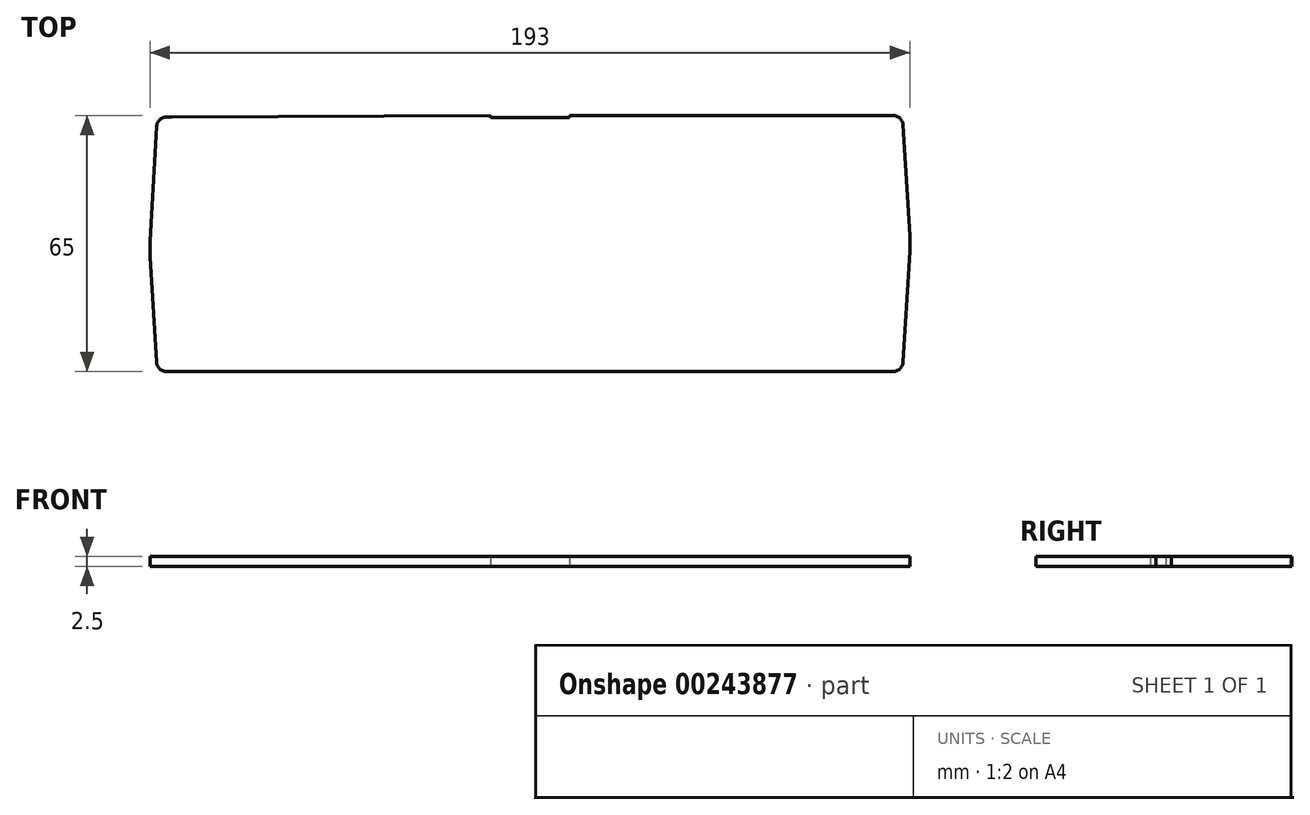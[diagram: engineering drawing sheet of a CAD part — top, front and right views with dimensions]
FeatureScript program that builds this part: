
annotation { "Feature Type Name" : "Feature", "Feature Type Description" : "" }
export const myFeature = defineFeature(function(context is Context, id is Id, definition is map)
    precondition{}
    {
        {
            var Q0;
            Q0=qCreatedBy(makeId("Top.planeOp"),FACE);
            var sketch = newSketch(context, id + "F0", { "sketchPlane" : qUnion([Q0])});
            skLineSegment(sketch, "E0", {"start": v(0, 0) * mm, "end": v(96.5, 0) * mm, "construction": true});
            skLineSegment(sketch, "E1", {"start": v(0, 0) * mm, "end": v(0, 32) * mm, "construction": true});
            skLineSegment(sketch, "E2", {"start": v(0, 0) * mm, "end": v(0, -32.5) * mm, "construction": true});
            skLineSegment(sketch, "E3", {"start": v(0, 32) * mm, "end": v(10, 32) * mm});
            skLineSegment(sketch, "E4", {"start": v(0, 32) * mm, "end": v(-10, 32) * mm});
            skLineSegment(sketch, "E5", {"start": v(-10, 32) * mm, "end": v(-10, 32.5) * mm});
            skLineSegment(sketch, "E6", {"start": v(10, 32) * mm, "end": v(10, 32.5) * mm});
            skLineSegment(sketch, "E7", {"start": v(0, -32.5) * mm, "end": v(92.28, -32.5) * mm});
            skLineSegment(sketch, "E8", {"start": v(0, -32.5) * mm, "end": v(-92.37, -32.5) * mm});
            skLineSegment(sketch, "E9", {"start": v(-96.5, -1.4) * mm, "end": v(-96.5, -3.4) * mm});
            skLineSegment(sketch, "E10", {"start": v(96.5, 0) * mm, "end": v(96.5, -2) * mm});
            skLineSegment(sketch, "E11", {"start": v(96.5, 0) * mm, "end": v(96.5, 2) * mm});
            skLineSegment(sketch, "E12", {"start": v(-10, 32.5) * mm, "end": v(-91.04, 32.14) * mm});
            skLineSegment(sketch, "E13", {"start": v(-96.5, -1.4) * mm, "end": v(-96.5, 0.6) * mm});
            skPoint(sketch, "E14.orphan", {"position": v(-122.96, 32) * mm});
            skLineSegment(sketch, "E15", {"start": v(10, 32.5) * mm, "end": v(92.28, 32.5) * mm});
            skLineSegment(sketch, "E16", {"start": v(-96.5, -3.4) * mm, "end": v(-94.86, -30.15) * mm});
            skLineSegment(sketch, "E17", {"start": v(96.5, 2) * mm, "end": v(94.78, 30.15) * mm});
            skLineSegment(sketch, "E18", {"start": v(96.5, -2) * mm, "end": v(94.78, -30.15) * mm});
            skPoint(sketch, "E19.visualSharp", {"position": v(94.63, -32.5) * mm});
            skArc(sketch, "E19.filletArc", {"start": v(92.28, -32.5) * mm, "mid": v(94, -31.82) * mm, "end": v(94.78, -30.15) * mm});
            skPoint(sketch, "E20.visualSharp", {"position": v(94.63, 32.5) * mm});
            skArc(sketch, "E20.filletArc", {"start": v(94.78, 30.15) * mm, "mid": v(94, 31.82) * mm, "end": v(92.28, 32.5) * mm});
            skPoint(sketch, "E21.visualSharp", {"position": v(-94.72, -32.5) * mm});
            skArc(sketch, "E21.filletArc", {"start": v(-94.86, -30.15) * mm, "mid": v(-94.08, -31.82) * mm, "end": v(-92.37, -32.5) * mm});
            skLineSegment(sketch, "E22", {"start": v(-91.04, 32.14) * mm, "end": v(-92.35, 32.14) * mm});
            skLineSegment(sketch, "E23", {"start": v(-96.5, 0.6) * mm, "end": v(-94.84, 29.78) * mm});
            skPoint(sketch, "E24.visualSharp", {"position": v(-94.71, 32.14) * mm});
            skArc(sketch, "E24.filletArc", {"start": v(-92.35, 32.14) * mm, "mid": v(-94.07, 31.46) * mm, "end": v(-94.84, 29.78) * mm});
            skSolve(sketch);
        }
        {
            var Q0;
            Q0=makeQuery(id+"F0.imprint","IMPRINT",FACE,{"disambiguationData":[TD([[makeQuery(id+"F0.imprint","IMPRINT",EDGE,{"derivedFrom":sQuery(id+"F0.wireOp",EDGE,"E3")}),-1.0]])]});
            extrude(context, id + "F1", {"entities" : qUnion([Q0]), "depth" : 2.5 * mm});
        }
    });
